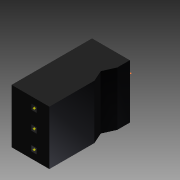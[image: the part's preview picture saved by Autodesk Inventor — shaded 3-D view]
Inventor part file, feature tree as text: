
AUTODESK INVENTOR PART (.ipt)
format: ipt  version: 2011 (Build 150239000, 239)  size: 119,296 bytes
history: native  units: in
note: dims shown in document units (in); Inventor stores cm internally (conversion verified against a paired STEP export)
features: other x12, plane x8, sketch x4, extrude x3
ambient origin geometry x8: Origin, YZ Plane, XZ Plane, XY Plane, X Axis, Y Axis, Z Axis, Center Point
bodies: Solid1 (feature_tree)
feature tree (27):
  extrude  "Extrusion1"  Depth=0.0241in
  sketch  "Sketch2"  dims[d3=1.0in d4=0.0in d5=0.125in]
  extrude  "Extrusion2"  Depth=0.125in
  other  "Work Point8"
  other  "Work Point9"
  other  "Work Point10"
  other  "Work Point11"
  other  "Work Point12"
  other  "Work Point13"
  extrude  "Extrusion3"  Depth=0.25in
  sketch  "Sketch1"  dims[d0=0.197in d1=0.0in d2=0.0241in]
  sketch  "Sketch3"  dims[d6=0.125in d7=0.25in]
  plane  "Work Plane5"
  plane  "Work Plane6"
  other  "Work Axis4"
  plane  "Work Plane7"
  plane  "Work Plane8"
  other  "Work Axis5"
  plane  "Work Plane9"
  other  "Work Axis6"
  plane  "Work Plane10"
  other  "Work Axis7"
  plane  "Work Plane11"
  other  "Work Axis8"
  plane  "Work Plane12"
  other  "Work Axis9"
  sketch  "Sketch4"  dims[d8=0.25in d9=0.125in d10=0.25in d11=0.125in d12=0.25in d13=0.25in d14=0.0in]
